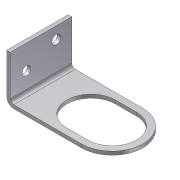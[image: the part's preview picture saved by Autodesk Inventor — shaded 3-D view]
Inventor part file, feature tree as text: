
AUTODESK INVENTOR PART (.ipt)
format: ipt  version: unknown  size: 209,408 bytes
history: native  units: mm (DEFAULTED — no unit token found)
features: sheet_metal_op x3, sketch x3, other x3, projected_geometry x1
ambient origin geometry x8: Origin, YZ Plane, XZ Plane, XY Plane, X Axis, Y Axis, Z Axis, Center Point
feature tree (10):
  sheet_metal_op  "Face1"
  sheet_metal_op  "Flange1"
  sketch  "Sketch1"  dims[d0=38.0mm]
  other  "Plate1"
  sketch  "Sketch2"  dims[d1=63.0mm]
  other  "Plate2"
  sheet_metal_op  "Bend1"
  sketch  "Sketch3"  dims[d2=4.0mm d3=43.0mm d4=2.2mm d5=2.2mm d6=1.1mm d7=4.4mm d8=2.2mm d9=27.0mm d10=90.0deg d11=2.2mm d12=5.5mm d13=9.5mm d14=7.5mm d15=10.0mm d16=15.0mm d17=2.2mm d18=0.0mm]
  projected_geometry  "Projected Loop1"
  other  "Cut1"
